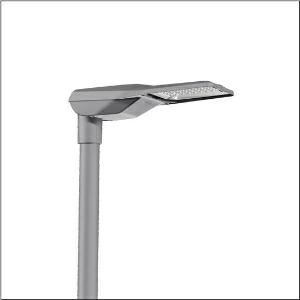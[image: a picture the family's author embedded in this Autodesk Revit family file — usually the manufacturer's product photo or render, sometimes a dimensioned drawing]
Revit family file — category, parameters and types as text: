
# Revit family: streetlight_sl_21_iq_mini___stw1_0a_5xe2e31g08gb_0d22
name_source: partatom
category: Lighting Fixtures
units: mm (PartAtom-declared; Revit-internal decimal feet)

## family parameters
Cut with Voids When Loaded = No
Host = Face
Light Source = No
Part Type = Normal
Room Calculation Point = No
Round Connector Dimension = Use Diameter
Shared = No

## types (1)
- --- (1 x LED, 5680 lm, 37.1 W, 3000K)
    Apparent Load = 37 VA
    CIE Flux Codes = 38 75 98 100 100
    Color Rendering = 70
    Color Temperature = 3000K
    Default Elevation = 1800 mm
    Description = Streetlight SL 21 iQ mini, mast luminaire, primary light control with lens, of PMMA, primary optical cover: cover, of toughened safety glass, transparent, light distribution: STW1.0a, light emission: direct distribution, primary light characteristic: asymmetric, installation type: post-top, side-entry, LED, High Power LED, rated luminous flux: 5.680lm, luminous efficacy: 153lm/W, light colour: 730, colour temperature: 3000K, control: Street-Remote, Auto-Match, Temp-Guard, Lumen-Switch, Night-Set, Smart-Wire, Light-Fading, Desk-Remote (wireless, voltage-free reading and setting of iQ features in the workshop via application-optimized NFC function/RFID function), optimised constant luminous flux control (CLO 2.0), pre-setting: linear dimming characteristic, mains connection: 220..240V, AC, 50/60Hz, start of lifetime: 37W, end of service life: 39W, reduction: 18W, luminaire housing, of diecast aluminium, powder-coated, Siteco® metallic grey (DB 702S), corrosivity category C5 mid according to DIN EN ISO 12944, please order mast flange separately, inclination adjustable: 0°, 5°, 10°, 15°, sealing non-destructively replaceable, multi-level sealing system, length: 628mm, width: 235mm, height: 110mm, mast flange for spigot size: 42mm (side-entry): 5XC10008XM4, 60/48mm (side-entry/post-top): 5XC10108XM2, 76/60mm (side-entry/post-top): 5XC10108XM1, protection rating (complete): IP66, insulation class (complete): insulation class II (safety insulation), certification: CE, ENEC, ENEC+, VDE, impact resistance: IK09, permissible operating ambient temperature for outdoor applications: -40..+50°C, standard-compliant lighting for roads and squares, packaging unit: 1 piece

Light Distribution: STW1.0a
    Height = 110 mm
    Lamp = 1 x LED
    Lamp Light Flux = 5680 lm
    Lamp Power = 37.1 W
    Lamp count = 1
    Length = 625 mm
    Luminous efficacy = 153 lm/W
    Manufacturer = Siteco
    ModVariant = No
    Model = 5XE2E31G08GB
    Number of Poles = 1
    OnlyDefault = Yes
    Power Factor = 1
    Product Name = Streetlight SL 21 iQ mini | STW1.0a
    Product group = mast luminaire | pylon top
    ProductGroupID = 6100
    Protection Class = Protection class II
    Protection Degree = IP 66
    RLX_Detail_Level = 1
    RLX_Emergency_Light_Flux = 0 lm
    RLX_Emergency_Type = 0
    RLX_Emergency_Type_DB = No
    RlxData = <blob elided: 92445 chars, md5=e7133835>
    Socket = socket
    Standby Power = 0 W
    System Light Flux = 5680 lm
    System Power = 37 W
    Type Comments = factory setting: luminous flux: 100 % | dim-lin: 254 | 385 mA
    Type Image = l_1003519.jpg
    URL = http://relux.com
    VarID = @adj_159445
    Voltage = 0 V
    Weight = 0.00 kg
    Width = 234 mm

## geometry (parser evidence)
native form markers: Blend x4, Sweep x12
no freeform markers — native parametric forms only
